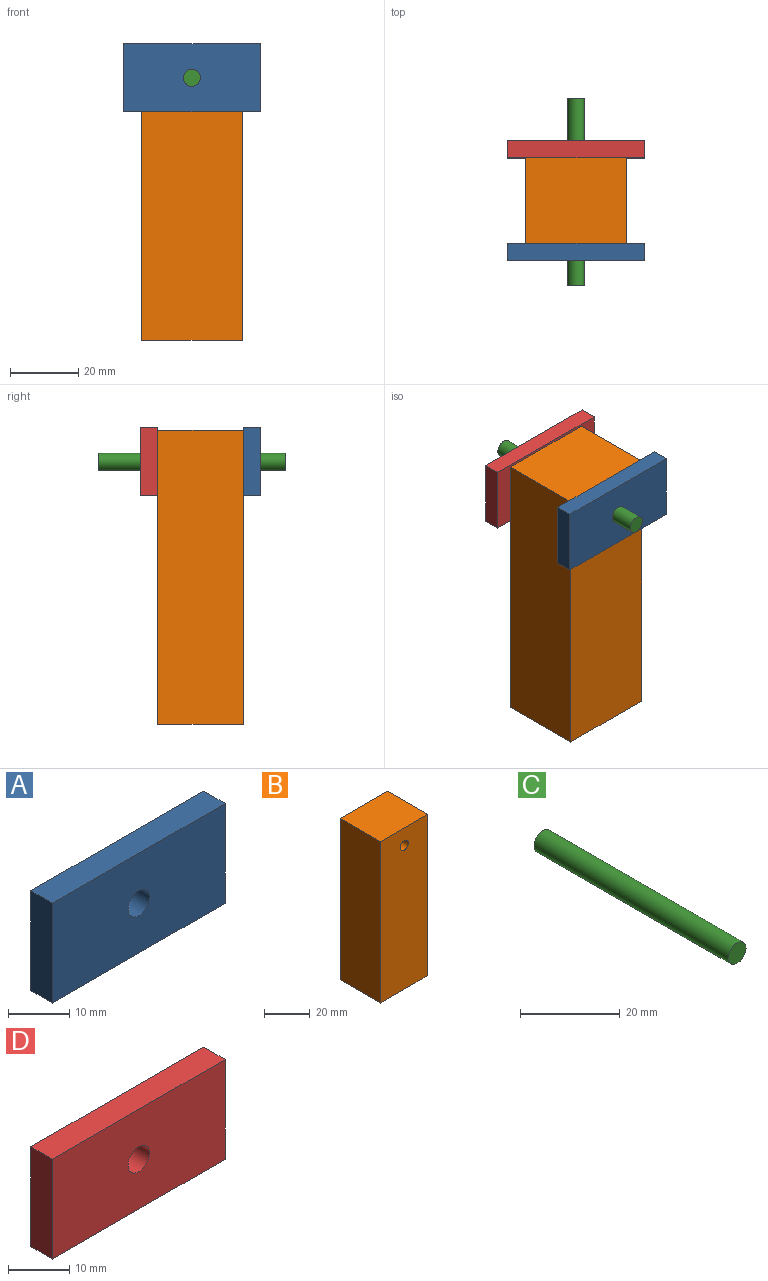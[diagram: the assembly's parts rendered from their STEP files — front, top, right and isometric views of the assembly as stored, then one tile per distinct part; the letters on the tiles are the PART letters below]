
ASSEMBLY  parts=4 mates=3
PART A: 7 faces, bbox 40x5x20 mm
  f0: plane 20x5mm, normal (-1,0,0), area 100mm2, adj f1,f4,f5,f6
  f1: plane 40x5mm, normal (0,0,-1), area 200mm2, adj f0,f2,f5,f6
  f2: plane 20x5mm, normal (1,0,0), area 100mm2, adj f1,f4,f5,f6
  f3: cylinder r=2.5mm len=5mm, axis (0,-1,0), area 78.5mm2, adj f5,f6
  f4: plane 40x5mm, normal (0,0,1), area 200mm2, adj f0,f2,f5,f6
  f5: plane 40x20mm, normal (0,1,0), area 780.4mm2, adj f0,f1,f2,f3,f4
  f6: plane 40x20mm, normal (0,-1,0), area 780.4mm2, adj f0,f1,f2,f3,f4
PART B: 7 faces, bbox 29.4x25x86.4 mm
  f0: plane 86.4x25mm, normal (-1,0,0), area 2159.9mm2, adj f1,f3,f4,f5
  f1: plane 29.44x25mm, normal (0,0,-1), area 735.9mm2, adj f0,f2,f4,f5
  f2: plane 86.4x25mm, normal (1,0,0), area 2159.9mm2, adj f1,f3,f4,f5
  f3: plane 29.44x25mm, normal (0,0,1), area 735.9mm2, adj f0,f2,f4,f5
  f4: plane 86.4x29.44mm, normal (0,-1,0), area 2523.5mm2, adj f0,f1,f2,f3,f6
  f5: plane 86.4x29.44mm, normal (0,1,0), area 2523.5mm2, adj f0,f1,f2,f3,f6
  f6: cylinder r=2.5mm len=25mm, axis (0,-1,0), area 392.7mm2, adj f4,f5
PART C: 3 faces, bbox 5x55x5 mm
  f0: cylinder r=2.5mm len=55mm, axis (0,1,0), area 863.9mm2, adj f1,f2
  f1: plane 5x5mm, normal (0,-1,0), area 19.6mm2, adj f0
  f2: plane 5x5mm, normal (0,1,0), area 19.6mm2, adj f0
PART D: 7 faces, bbox 40x5x20 mm
  f0: plane 20x5mm, normal (-1,0,0), area 100mm2, adj f1,f4,f5,f6
  f1: plane 40x5mm, normal (0,0,-1), area 200mm2, adj f0,f2,f5,f6
  f2: plane 20x5mm, normal (1,0,0), area 100mm2, adj f1,f4,f5,f6
  f3: cylinder r=2.5mm len=5mm, axis (0,-1,0), area 78.5mm2, adj f5,f6
  f4: plane 40x5mm, normal (0,0,1), area 200mm2, adj f0,f2,f5,f6
  f5: plane 40x20mm, normal (0,1,0), area 780.4mm2, adj f0,f1,f2,f3,f4
  f6: plane 40x20mm, normal (0,-1,0), area 780.4mm2, adj f0,f1,f2,f3,f4
PLACE A t=(34.85,-39.57,54.97)mm
PLACE B t=(-18.51,-9.57,24.73)mm
PLACE C t=(-56,-7.07,4.93)mm
PLACE D t=(31.85,-9.57,28.6)mm
MATE revolute D.f3 <-> B.f6  axis (0,-1,0) through (-18.51,-9.57,58.61)mm
MATE revolute C.f0 <-> B.f6  axis (0,1,0) through (-18.51,-19.57,58.61)mm
MATE revolute A.f3 <-> B.f6  axis (0,1,0) through (-18.51,-34.57,58.61)mm
